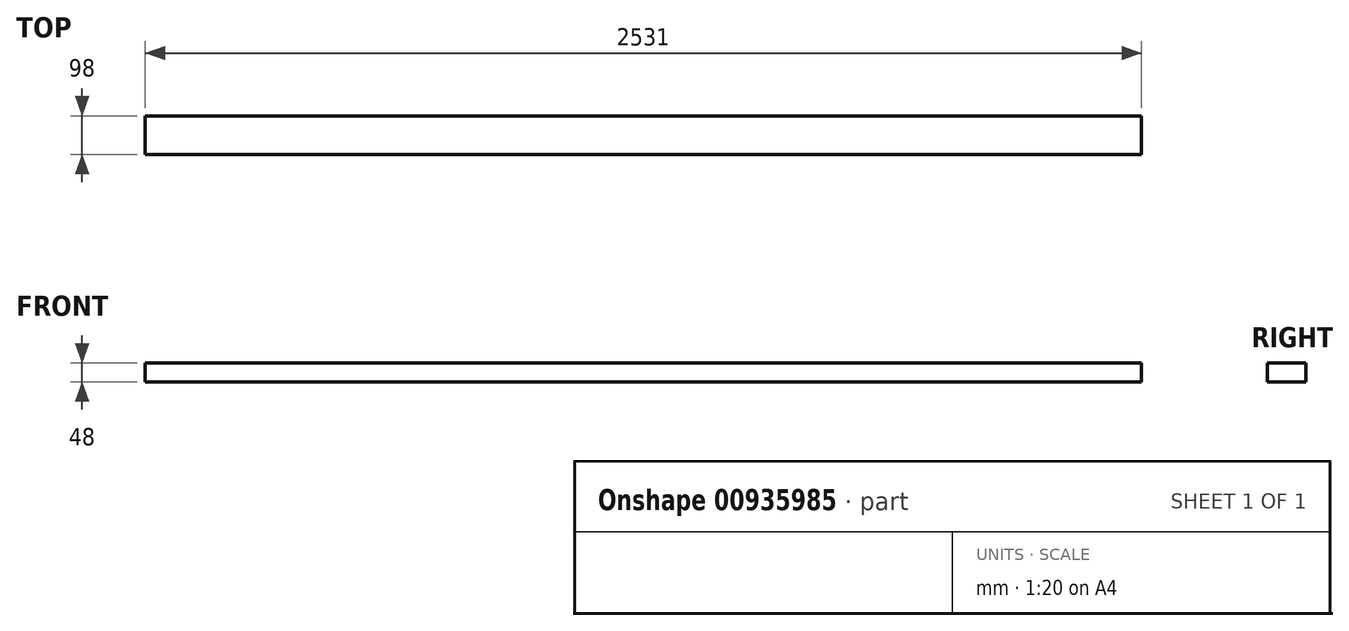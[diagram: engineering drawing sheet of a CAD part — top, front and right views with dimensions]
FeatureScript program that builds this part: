
annotation { "Feature Type Name" : "Feature", "Feature Type Description" : "" }
export const myFeature = defineFeature(function(context is Context, id is Id, definition is map)
    precondition{}
    {
        {
            var Q0;
            Q0=qCreatedBy(makeId("Right.planeOp"),FACE);
            var sketch = newSketch(context, id + "F0", { "sketchPlane" : qUnion([Q0])});
            skLineSegment(sketch, "E0.bottom", {"start": v(49, -24) * mm, "end": v(-49, -24) * mm});
            skLineSegment(sketch, "E0.top", {"start": v(49, 24) * mm, "end": v(-49, 24) * mm});
            skLineSegment(sketch, "E0.left", {"start": v(49, -24) * mm, "end": v(49, 24) * mm});
            skLineSegment(sketch, "E0.right", {"start": v(-49, -24) * mm, "end": v(-49, 24) * mm});
            skPoint(sketch, "E0.middle", {"position": v(0, 0) * mm});
            skSolve(sketch);
        }
        {
            assignVariable(context, id + "F1", {"name" : "Length", "anyValue" : 2531});
        }
        {
            var Q0;
            Q0 = qSketchRegion(id + "F0", true);
            extrude(context, id + "F2", {"entities" : qUnion([Q0]), "depth" : (getVariable(context, 'Length')) * mm, "offsetDistance" : 25 * mm});
        }
    });
